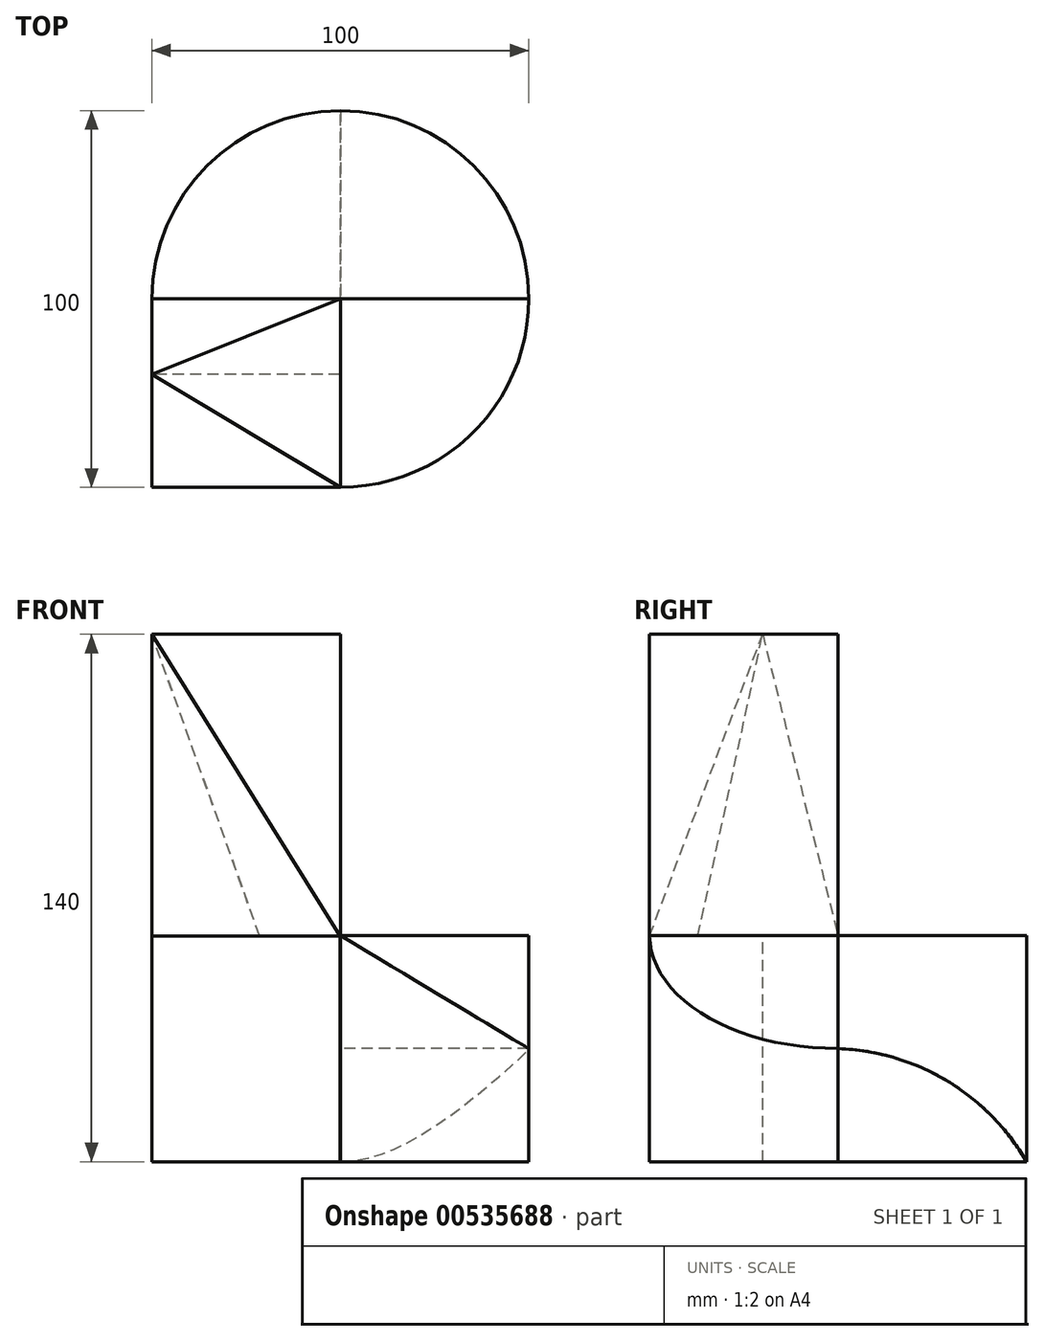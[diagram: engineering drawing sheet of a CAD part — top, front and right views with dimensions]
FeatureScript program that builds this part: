
annotation { "Feature Type Name" : "Feature", "Feature Type Description" : "" }
export const myFeature = defineFeature(function(context is Context, id is Id, definition is map)
    precondition{}
    {
        {
            var Q0;
            Q0=qCreatedBy(makeId("Front.planeOp"),FACE);
            var sketch = newSketch(context, id + "F0", { "sketchPlane" : qUnion([Q0])});
            skLineSegment(sketch, "E0.bottom", {"start": v(0, 0) * mm, "end": v(-100, 0) * mm});
            skLineSegment(sketch, "E0.top", {"start": v(0, 140) * mm, "end": v(-100, 140) * mm});
            skLineSegment(sketch, "E0.left", {"start": v(0, 0) * mm, "end": v(0, 140) * mm});
            skLineSegment(sketch, "E0.right", {"start": v(-100, 0) * mm, "end": v(-100, 140) * mm});
            skSolve(sketch);
        }
        {
            var Q0;
            Q0=makeQuery(id+"F0.imprint","IMPRINT",FACE,{"disambiguationData":[TD([[makeQuery(id+"F0.imprint","IMPRINT",EDGE,{"derivedFrom":sQuery(id+"F0.wireOp",EDGE,"E0.bottom")}),-1.0]])]});
            extrude(context, id + "F1", {"entities" : qUnion([Q0]), "depth" : 100 * mm, "offsetDistance" : 25 * mm});
        }
        {
            var Q0;
            Q0=makeQuery(id+"F1.opExtrude","CAP_EDGE",EDGE,{"disambiguationData":[OSD([sQuery(id+"F0.wireOp",EDGE,"E0.left")])],"isStart":false});
            fillet(context, id + "F2", {"entities" : qUnion([Q0]), "radius" : 50 * mm, "tangentPropagation" : true, "allowEdgeOverflow" : false});
        }
        {
            var Q0;
            Q0=makeQuery(id+"F1.opExtrude","CAP_EDGE",EDGE,{"disambiguationData":[OSD([sQuery(id+"F0.wireOp",EDGE,"E0.left")])],"isStart":true});
            fillet(context, id + "F3", {"entities" : qUnion([Q0]), "radius" : 50 * mm, "tangentPropagation" : true, "allowEdgeOverflow" : false});
        }
        {
            var Q0;
            Q0=makeQuery(id+"F1.opExtrude","CAP_EDGE",EDGE,{"disambiguationData":[OSD([sQuery(id+"F0.wireOp",EDGE,"E0.right")])],"isStart":true});
            fillet(context, id + "F4", {"entities" : qUnion([Q0]), "radius" : 50 * mm, "tangentPropagation" : true, "allowEdgeOverflow" : false});
        }
        {
            var Q0;
            Q0=makeQuery(id+"F1.opExtrude","SWEPT_FACE",FACE,{"disambiguationData":[OSD([sQuery(id+"F0.wireOp",EDGE,"E0.top")])]});
            var sketch = newSketch(context, id + "F5", { "sketchPlane" : qUnion([Q0])});
            skLineSegment(sketch, "E1.bottom", {"start": v(-100, -100) * mm, "end": v(-50, -100) * mm});
            skLineSegment(sketch, "E1.top", {"start": v(-100, -50) * mm, "end": v(-50, -50) * mm});
            skLineSegment(sketch, "E1.left", {"start": v(-100, -100) * mm, "end": v(-100, -50) * mm});
            skLineSegment(sketch, "E1.right", {"start": v(-50, -100) * mm, "end": v(-50, -50) * mm});
            skSolve(sketch);
        }
        {
            var Q0;
            Q0=makeQuery(id+"F5.imprint","IMPRINT",FACE,{"disambiguationData":[TD([[makeQuery(id+"F5.imprint","IMPRINT",EDGE,{"derivedFrom":sQuery(id+"F5.wireOp",EDGE,"E1.top")}),1.0]])]});
            extrude(context, id + "F6", {"entities" : qUnion([Q0]), "operationType" : NewBodyOperationType.REMOVE, "oppositeDirection" : true, "depth" : 80 * mm, "offsetDistance" : 25 * mm});
        }
        {
            var Q0;
            Q0=makeQuery(id+"F1.opExtrude","SWEPT_FACE",FACE,{"disambiguationData":[OSD([sQuery(id+"F0.wireOp",EDGE,"E0.top")])]});
            var sketch = newSketch(context, id + "F7", { "sketchPlane" : qUnion([Q0])});
            skLineSegment(sketch, "E2", {"start": v(-100, -70) * mm, "end": v(-50, -70) * mm, "construction": true});
            skLineSegment(sketch, "E3", {"start": v(-50, -50) * mm, "end": v(-100, -70) * mm});
            skLineSegment(sketch, "E4", {"start": v(-50, -100) * mm, "end": v(-100, -70) * mm});
            skSolve(sketch);
        }
        {
            var Q0;
            Q0=makeQuery(id+"F1.opExtrude","CAP_FACE",FACE,{"disambiguationData":[OSD([sQuery(id+"F0.wireOp",EDGE,"E0.bottom"),sQuery(id+"F0.wireOp",EDGE,"E0.top"),sQuery(id+"F0.wireOp",EDGE,"E0.left"),sQuery(id+"F0.wireOp",EDGE,"E0.right")])],"isStart":false});
            var sketch = newSketch(context, id + "F8", { "sketchPlane" : qUnion([Q0])});
            skLineSegment(sketch, "E5.bottom", {"start": v(-100, 0) * mm, "end": v(-50.1, 0) * mm});
            skLineSegment(sketch, "E5.top", {"start": v(-100, 59.9) * mm, "end": v(-50.1, 59.9) * mm});
            skLineSegment(sketch, "E5.left", {"start": v(-100, 0) * mm, "end": v(-100, 59.9) * mm});
            skLineSegment(sketch, "E5.right", {"start": v(-50.1, 0) * mm, "end": v(-50.1, 59.9) * mm});
            skSolve(sketch);
        }
        {
            var Q0;
            Q0=makeQuery(id+"F8.imprint","IMPRINT",FACE,{"disambiguationData":[TD([[makeQuery(id+"F8.imprint","IMPRINT",EDGE,{"derivedFrom":sQuery(id+"F8.wireOp",EDGE,"E5.bottom")}),-1.0]])]});
            extrude(context, id + "F9", {"entities" : qUnion([Q0]), "operationType" : NewBodyOperationType.REMOVE, "oppositeDirection" : true, "depth" : 30 * mm, "offsetDistance" : 25 * mm});
        }
        {
            var Q1;
            {var subQ0=sQuery(id+"F7.wireOp",EDGE,"E3");Q1=makeQuery(id+"F7.imprint","IMPRINT",FACE,{"disambiguationData":[TD([[makeQuery(id+"F7.imprint","IMPRINT",EDGE,{"derivedFrom":subQ0}),-1.0]])]});}
            var Q2;
            Q2=makeQuery(id+"F6.boolean.opBoolean","COPY",VERTEX,{"derivedFrom":makeQuery(id+"F6.opExtrude","CAP_VERTEX",VERTEX,{"disambiguationData":[OSD([sQuery(id+"F5.wireOp",EDGE,"E1.top"),sQuery(id+"F5.wireOp",EDGE,"E1.right")])],"isStart":false})});
            loft(context, id + "F10", {"operationType" : NewBodyOperationType.REMOVE, "sheetProfilesArray" : [{ "sheetProfileEntities" : qUnion([Q1]) }, { "sheetProfileEntities" : qUnion([Q2]) }]});
        }
        {
            var Q0;
            Q0=makeQuery(id+"F1.opExtrude","CAP_FACE",FACE,{"disambiguationData":[OSD([sQuery(id+"F0.wireOp",EDGE,"E0.bottom"),sQuery(id+"F0.wireOp",EDGE,"E0.top"),sQuery(id+"F0.wireOp",EDGE,"E0.left"),sQuery(id+"F0.wireOp",EDGE,"E0.right")])],"isStart":false});
            var sketch = newSketch(context, id + "F11", { "sketchPlane" : qUnion([Q0])});
            skLineSegment(sketch, "E6", {"start": v(-100, 140) * mm, "end": v(-50, 60) * mm});
            skSolve(sketch);
        }
        {
            var Q1;
            Q1=makeQuery(id+"F11.imprint","IMPRINT",FACE,{"disambiguationData":[TD([[makeQuery(id+"F11.imprint","IMPRINT",EDGE,{"derivedFrom":sQuery(id+"F11.wireOp",EDGE,"E6")}),-1.0]])]});
            var Q2;
            Q2=sQuery(id+"F7.wireOp",VERTEX,"E4.end");
            loft(context, id + "F12", {"operationType" : NewBodyOperationType.REMOVE, "sheetProfilesArray" : [{ "sheetProfileEntities" : qUnion([Q1]) }, { "sheetProfileEntities" : qUnion([Q2]) }]});
        }
        {
            var Q1;
            {var subQ0=sQuery(id+"F7.wireOp",EDGE,"E4");Q1=makeQuery(id+"F7.imprint","IMPRINT",FACE,{"disambiguationData":[TD([[makeQuery(id+"F7.imprint","IMPRINT",EDGE,{"derivedFrom":subQ0}),1.0]])]});}
            var Q2;
            {var subQ0=sQuery(id+"F5.wireOp",EDGE,"E1.right");var subQ1=sQuery(id+"F5.wireOp",EDGE,"E1.bottom");var subQ2=sQuery(id+"F0.wireOp",EDGE,"E0.left");var subQ3=sQuery(id+"F0.wireOp",EDGE,"E0.top");Q2=makeQuery(id+"F12.boolean.opBoolean","MERGE",VERTEX,{"derivedFrom":[makeQuery(id+"F6.boolean.opBoolean","COPY",VERTEX,{"derivedFrom":makeQuery(id+"F6.opExtrude","CAP_VERTEX",VERTEX,{"disambiguationData":[OSD([subQ3,subQ2,subQ1,subQ0])],"isStart":false})}),makeQuery(id+"F12.opLoft","MID_CAP_VERTEX",VERTEX,{"disambiguationData":[OSD([sQuery(id+"F0.wireOp",EDGE,"E0.bottom"),subQ3,subQ2,sQuery(id+"F0.wireOp",EDGE,"E0.right"),subQ1,subQ0,sQuery(id+"F11.wireOp",EDGE,"E6")])],"capPos":0.0})]});}
            loft(context, id + "F13", {"operationType" : NewBodyOperationType.REMOVE, "sheetProfilesArray" : [{ "sheetProfileEntities" : qUnion([Q1]) }, { "sheetProfileEntities" : qUnion([Q2]) }]});
        }
        {
            var Q0;
            Q0=makeQuery(id+"F6.boolean.opBoolean","COPY",FACE,{"derivedFrom":makeQuery(id+"F6.opExtrude","CAP_FACE",FACE,{"disambiguationData":[OSD([sQuery(id+"F0.wireOp",EDGE,"E0.top"),sQuery(id+"F0.wireOp",EDGE,"E0.left"),sQuery(id+"F0.wireOp",EDGE,"E0.right"),sQuery(id+"F5.wireOp",EDGE,"E1.top"),sQuery(id+"F5.wireOp",EDGE,"E1.right")])],"isStart":false})});
            var sketch = newSketch(context, id + "F14", { "sketchPlane" : qUnion([Q0])});
            skLineSegment(sketch, "E7", {"start": v(-50, -50) * mm, "end": v(0, -50) * mm});
            skSolve(sketch);
        }
        {
            var Q0;
            Q0=qCreatedBy(makeId("Front.planeOp"),FACE);
            var Q1;
            Q1=sQuery(id+"F14.wireOp",VERTEX,"E7.start");
            cPlane(context, id + "F15", {"entities" : qUnion([Q0, Q1]), "cplaneType" : CPlaneType.PLANE_POINT, "offset" : 25 * mm, "width" : 150 * mm, "height" : 150 * mm});
        }
        {
            var Q0;
            Q0=qCreatedBy(id+"F15.planeOp",FACE);
            var sketch = newSketch(context, id + "F16", { "sketchPlane" : qUnion([Q0])});
            skLineSegment(sketch, "E8", {"start": v(-50, 60) * mm, "end": v(0, 60) * mm});
            skLineSegment(sketch, "E9", {"start": v(0, 60) * mm, "end": v(0, 30) * mm});
            skLineSegment(sketch, "E10", {"start": v(0, 30) * mm, "end": v(-50, 60) * mm});
            skSolve(sketch);
        }
        {
            var Q0;
            Q0 = qSketchRegion(id + "F16", true);
            extrude(context, id + "F17", {"entities" : qUnion([Q0]), "operationType" : NewBodyOperationType.REMOVE, "endBound" : BoundingType.UP_TO_NEXT, "depth" : 25 * mm, "offsetDistance" : 25 * mm});
        }
        {
            var Q0;
            Q0=qCreatedBy(makeId("Right.planeOp"),FACE);
            var Q1;
            {var subQ0=sQuery(id+"F7.wireOp",EDGE,"E3");var subQ1=sQuery(id+"F5.wireOp",EDGE,"E1.right");var subQ2=sQuery(id+"F5.wireOp",EDGE,"E1.top");Q1=makeQuery(id+"F17.boolean.opBoolean","MERGE",VERTEX,{"derivedFrom":[makeQuery(id+"F10.boolean.opBoolean","MERGE",VERTEX,{"derivedFrom":[makeQuery(id+"F6.boolean.opBoolean","COPY",VERTEX,{"derivedFrom":makeQuery(id+"F6.opExtrude","CAP_VERTEX",VERTEX,{"disambiguationData":[OSD([subQ2,subQ1])],"isStart":false})}),makeQuery(id+"F10.opLoft","SWEPT_VERTEX",VERTEX,{"disambiguationData":[OSD([subQ2,subQ1,subQ0])]})]}),makeQuery(id+"F17.opExtrude","CAP_VERTEX",VERTEX,{"disambiguationData":[OSD([subQ2,subQ1,subQ0,sQuery(id+"F16.wireOp",EDGE,"E8"),sQuery(id+"F16.wireOp",EDGE,"E10")])],"isStart":true})]});}
            cPlane(context, id + "F18", {"entities" : qUnion([Q0, Q1]), "cplaneType" : CPlaneType.PLANE_POINT, "offset" : 25 * mm, "width" : 150 * mm, "height" : 150 * mm});
        }
        {
            var Q0;
            Q0=qCreatedBy(id+"F18.planeOp",FACE);
            var sketch = newSketch(context, id + "F19", { "sketchPlane" : qUnion([Q0])});
            skArc(sketch, "E11", {"start": v(0, 0) * mm, "mid": v(-21.11, 21.48) * mm, "end": v(-50, 30) * mm});
            skLineSegment(sketch, "E12", {"start": v(-50, 30) * mm, "end": v(-50, 0) * mm});
            skLineSegment(sketch, "E13", {"start": v(-50, 0) * mm, "end": v(0, 0) * mm});
            skSolve(sketch);
        }
        {
            var Q0;
            Q0 = qSketchRegion(id + "F19", true);
            extrude(context, id + "F20", {"entities" : qUnion([Q0]), "operationType" : NewBodyOperationType.REMOVE, "endBound" : BoundingType.UP_TO_NEXT, "depth" : 25 * mm, "offsetDistance" : 25 * mm});
        }
    });
